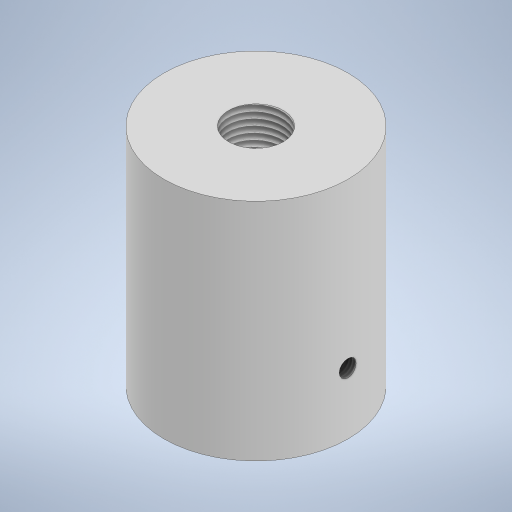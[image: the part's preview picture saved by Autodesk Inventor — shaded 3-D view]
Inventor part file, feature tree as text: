
AUTODESK INVENTOR PART (.ipt)
format: ipt  version: 2023 (Build 270158000, 158)  size: 251,904 bytes
history: native  units: mm
features: sketch x6, hole x3, other x2, extrude x2
ambient origin geometry x8: Origin, YZ Plane, XZ Plane, XY Plane, X Axis, Y Axis, Z Axis, Center Point
bodies: Body1 (feature_tree)
feature tree (13):
  other  "Твердое тело1"
  extrude  "Выдавливание1"  Depth=45.0mm
  sketch  "Эскиз2"
  other  "РабПлоскость1"
  hole  "Отверстие1"  [1 undecoded]
  hole  "Отверстие2"  [1 undecoded]
  extrude  "Выдавливание2"  Depth=5.0mm
  hole  "Отверстие3"  [1 undecoded]
  sketch  "Эскиз1"
  sketch  "Эскиз3"
  sketch  "Эскиз4"
  sketch  "Эскиз5"
  sketch  "Эскиз6"
note: 3 required parameter values undecoded (feature->parameter linkage not recoverable at this tier; creation-order binding heuristic only, values carry confidence <= 0.55)
